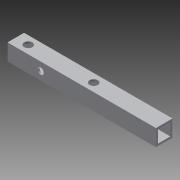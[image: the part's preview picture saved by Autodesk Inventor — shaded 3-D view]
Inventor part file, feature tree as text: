
AUTODESK INVENTOR PART (.ipt)
format: ipt  version: 2014 (Build 180170000, 170)  size: 118,272 bytes
history: native  units: in
note: dims shown in document units (in); Inventor stores cm internally (conversion verified against a paired STEP export)
features: sketch x4, extrude x3, hole x1
ambient origin geometry x8: Origin, YZ Plane, XZ Plane, XY Plane, X Axis, Y Axis, Z Axis, Center Point
bodies: Solid1 (feature_tree)
feature tree (8):
  extrude  "Extrusion1"  Depth=1.0in
  extrude  "Extrusion2"  Depth=8.95in TaperAngle=0.0deg
  extrude  "Extrusion3"  Depth=0.5in
  hole  "Hole1"  [1 undecoded]
  sketch  "Sketch1"  dims[d0=1.0in d1=1.0in]
  sketch  "Sketch2"  dims[d2=0.125in d3=8.95in d4=0.0in]
  sketch  "Sketch3"  dims[d5=0.5in d6=0.5in]
  sketch  "Sketch4"  dims[d7=0.75in d8=1.0in d9=0.0in d10=0.375in d11=2.0in d12=0.5in d13=1.0in d14=0.0in d15=0.5in d16=4.25in d17=0.5in d18=0.75in d19=0.375in d20=0.25in d21=0.5635in d22=1.0in d23=0.8108in]
note: 1 required parameter value undecoded (feature->parameter linkage not recoverable at this tier; creation-order binding heuristic only, values carry confidence <= 0.55)
